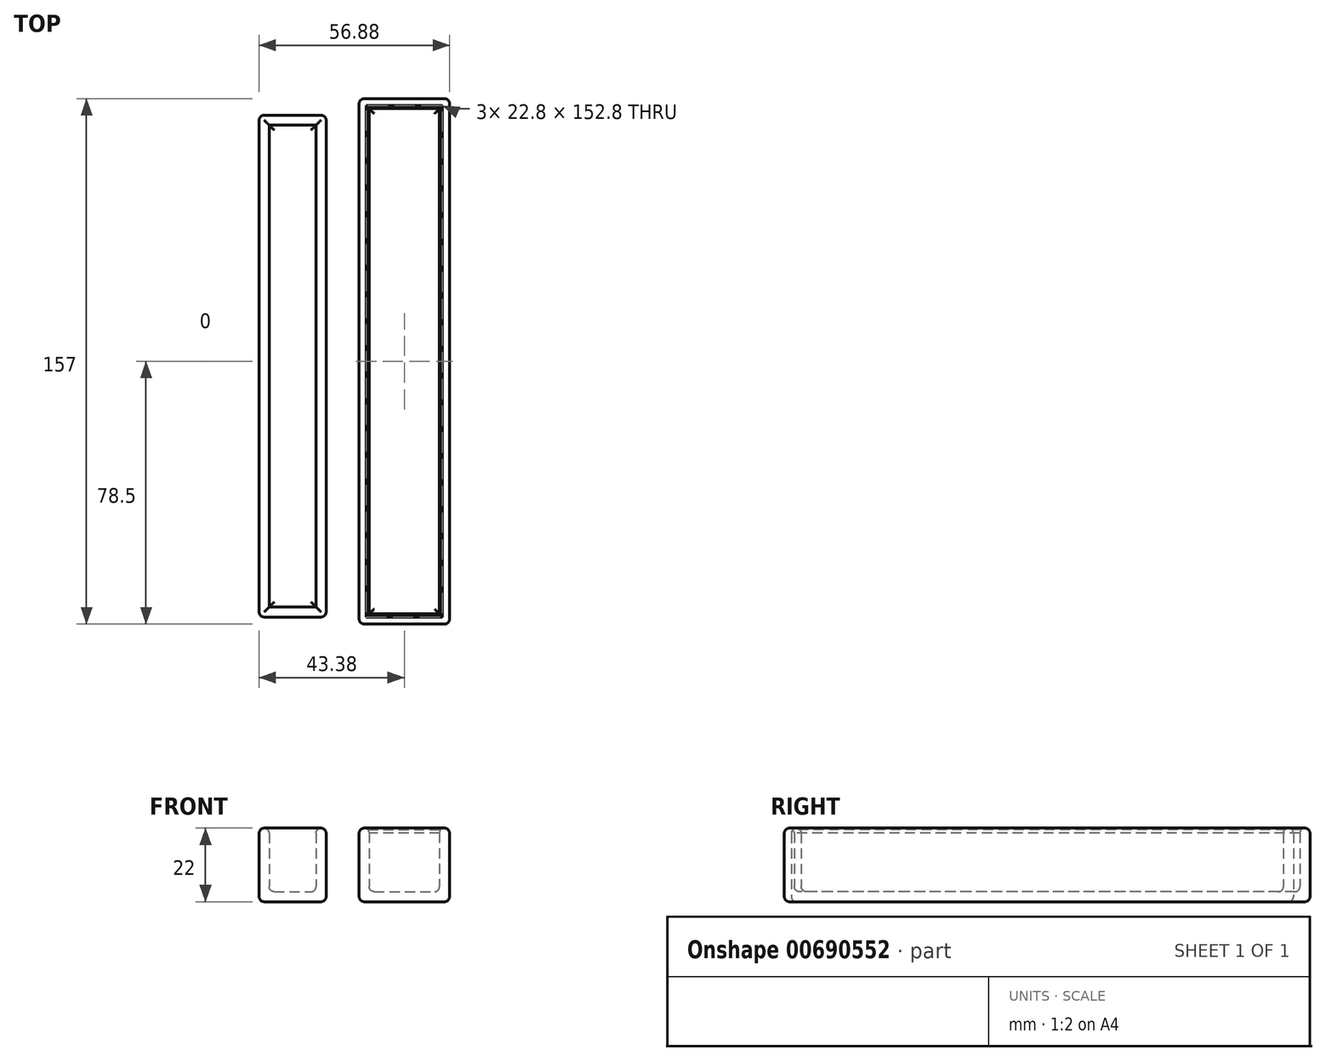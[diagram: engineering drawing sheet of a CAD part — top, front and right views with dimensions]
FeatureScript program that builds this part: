
annotation { "Feature Type Name" : "Feature", "Feature Type Description" : "" }
export const myFeature = defineFeature(function(context is Context, id is Id, definition is map)
    precondition{}
    {
        {
            var Q0;
            Q0=qCreatedBy(makeId("Top.planeOp"),FACE);
            var sketch = newSketch(context, id + "F0", { "sketchPlane" : qUnion([Q0])});
            skLineSegment(sketch, "E0.bottom", {"start": v(-39.88, 77.07) * mm, "end": v(-19.88, 77.07) * mm});
            skLineSegment(sketch, "E0.top", {"start": v(-39.88, -72.93) * mm, "end": v(-19.88, -72.93) * mm});
            skLineSegment(sketch, "E0.left", {"start": v(-39.88, 77.07) * mm, "end": v(-39.88, -72.93) * mm});
            skLineSegment(sketch, "E0.right", {"start": v(-19.88, 77.07) * mm, "end": v(-19.88, -72.93) * mm});
            skSolve(sketch);
        }
        {
            var Q0;
            Q0 = qSketchRegion(id + "F0", true);
            extrude(context, id + "F1", {"entities" : qUnion([Q0]), "depth" : 22 * mm, "offsetDistance" : 25 * mm});
        }
        {
            var Q0;
            Q0=makeQuery(id+"F1.opExtrude","CAP_FACE",FACE,{"disambiguationData":[OSD([sQuery(id+"F0.wireOp",EDGE,"E0.bottom"),sQuery(id+"F0.wireOp",EDGE,"E0.top"),sQuery(id+"F0.wireOp",EDGE,"E0.left"),sQuery(id+"F0.wireOp",EDGE,"E0.right")])],"isStart":false});
            shell(context, id + "F2", {"entities" : qUnion([Q0]), "thickness" : 3 * mm});
        }
        {
            var Q0;
            Q0=qCreatedBy(makeId("Top.planeOp"),FACE);
            var sketch = newSketch(context, id + "F3", { "sketchPlane" : qUnion([Q0])});
            skLineSegment(sketch, "E1.bottom", {"start": v(-10, 82) * mm, "end": v(17, 82) * mm});
            skLineSegment(sketch, "E1.top", {"start": v(-10, -75) * mm, "end": v(17, -75) * mm});
            skLineSegment(sketch, "E1.left", {"start": v(-10, 82) * mm, "end": v(-10, -75) * mm});
            skLineSegment(sketch, "E1.right", {"start": v(17, 82) * mm, "end": v(17, -75) * mm});
            skSolve(sketch);
        }
        {
            var Q0;
            Q0=makeQuery(id+"F3.imprint","IMPRINT",FACE,{"disambiguationData":[TD([[makeQuery(id+"F3.imprint","IMPRINT",EDGE,{"derivedFrom":sQuery(id+"F3.wireOp",EDGE,"E1.bottom")}),-1.0]])]});
            extrude(context, id + "F4", {"entities" : qUnion([Q0]), "depth" : 22 * mm, "offsetDistance" : 25 * mm});
        }
        {
            var Q0;
            Q0=makeQuery(id+"F4.opExtrude","CAP_FACE",FACE,{"disambiguationData":[OSD([sQuery(id+"F3.wireOp",EDGE,"E1.bottom"),sQuery(id+"F3.wireOp",EDGE,"E1.top"),sQuery(id+"F3.wireOp",EDGE,"E1.left"),sQuery(id+"F3.wireOp",EDGE,"E1.right")])],"isStart":false});
            shell(context, id + "F5", {"entities" : qUnion([Q0]), "thickness" : 3 * mm});
        }
        {
            var Q0;
            Q0=makeQuery(id+"F1.opExtrude","CAP_EDGE",EDGE,{"disambiguationData":[OSD([sQuery(id+"F0.wireOp",EDGE,"E0.right")])],"isStart":false});
            var Q1;
            {var subQ0=sQuery(id+"F0.wireOp",EDGE,"E0.right");Q1=makeQuery(id+"F2.opShell","OFFSET_EDGE",EDGE,{"disambiguationData":[OSD([subQ0]),TDD([makeQuery(id+"F1.opExtrude","CAP_EDGE",EDGE,{"disambiguationData":[OSD([subQ0])],"isStart":false})])]});}
            var Q2;
            Q2=makeQuery(id+"F1.opExtrude","CAP_EDGE",EDGE,{"disambiguationData":[OSD([sQuery(id+"F0.wireOp",EDGE,"E0.bottom")])],"isStart":false});
            var Q3;
            {var subQ0=sQuery(id+"F0.wireOp",EDGE,"E0.bottom");Q3=makeQuery(id+"F2.opShell","OFFSET_EDGE",EDGE,{"disambiguationData":[OSD([subQ0]),TDD([makeQuery(id+"F1.opExtrude","CAP_EDGE",EDGE,{"disambiguationData":[OSD([subQ0])],"isStart":false})])]});}
            var Q4;
            Q4=makeQuery(id+"F1.opExtrude","CAP_EDGE",EDGE,{"disambiguationData":[OSD([sQuery(id+"F0.wireOp",EDGE,"E0.left")])],"isStart":false});
            var Q5;
            {var subQ0=sQuery(id+"F0.wireOp",EDGE,"E0.left");Q5=makeQuery(id+"F2.opShell","OFFSET_EDGE",EDGE,{"disambiguationData":[OSD([subQ0]),TDD([makeQuery(id+"F1.opExtrude","CAP_EDGE",EDGE,{"disambiguationData":[OSD([subQ0])],"isStart":false})])]});}
            var Q6;
            {var subQ0=sQuery(id+"F0.wireOp",EDGE,"E0.top");Q6=makeQuery(id+"F2.opShell","OFFSET_EDGE",EDGE,{"disambiguationData":[OSD([subQ0]),TDD([makeQuery(id+"F1.opExtrude","CAP_EDGE",EDGE,{"disambiguationData":[OSD([subQ0])],"isStart":false})])]});}
            var Q7;
            Q7=makeQuery(id+"F1.opExtrude","CAP_EDGE",EDGE,{"disambiguationData":[OSD([sQuery(id+"F0.wireOp",EDGE,"E0.top")])],"isStart":false});
            var Q8;
            Q8=makeQuery(id+"F1.opExtrude","CAP_EDGE",EDGE,{"disambiguationData":[OSD([sQuery(id+"F0.wireOp",EDGE,"E0.left")])],"isStart":true});
            var Q9;
            Q9=makeQuery(id+"F1.opExtrude","SWEPT_EDGE",EDGE,{"disambiguationData":[OSD([sQuery(id+"F0.wireOp",EDGE,"E0.top"),sQuery(id+"F0.wireOp",EDGE,"E0.left")])]});
            var Q10;
            Q10=makeQuery(id+"F1.opExtrude","CAP_EDGE",EDGE,{"disambiguationData":[OSD([sQuery(id+"F0.wireOp",EDGE,"E0.top")])],"isStart":true});
            var Q11;
            Q11=makeQuery(id+"F1.opExtrude","SWEPT_EDGE",EDGE,{"disambiguationData":[OSD([sQuery(id+"F0.wireOp",EDGE,"E0.top"),sQuery(id+"F0.wireOp",EDGE,"E0.right")])]});
            var Q12;
            Q12=makeQuery(id+"F1.opExtrude","SWEPT_EDGE",EDGE,{"disambiguationData":[OSD([sQuery(id+"F0.wireOp",EDGE,"E0.bottom"),sQuery(id+"F0.wireOp",EDGE,"E0.right")])]});
            var Q13;
            Q13=makeQuery(id+"F1.opExtrude","SWEPT_EDGE",EDGE,{"disambiguationData":[OSD([sQuery(id+"F0.wireOp",EDGE,"E0.bottom"),sQuery(id+"F0.wireOp",EDGE,"E0.left")])]});
            var Q14;
            Q14=makeQuery(id+"F1.opExtrude","CAP_EDGE",EDGE,{"disambiguationData":[OSD([sQuery(id+"F0.wireOp",EDGE,"E0.bottom")])],"isStart":true});
            var Q15;
            Q15=makeQuery(id+"F1.opExtrude","CAP_EDGE",EDGE,{"disambiguationData":[OSD([sQuery(id+"F0.wireOp",EDGE,"E0.right")])],"isStart":true});
            var Q16;
            Q16=makeQuery(id+"F4.opExtrude","CAP_EDGE",EDGE,{"disambiguationData":[OSD([sQuery(id+"F3.wireOp",EDGE,"E1.bottom")])],"isStart":false});
            var Q17;
            Q17=makeQuery(id+"F4.opExtrude","CAP_EDGE",EDGE,{"disambiguationData":[OSD([sQuery(id+"F3.wireOp",EDGE,"E1.left")])],"isStart":false});
            var Q18;
            Q18=makeQuery(id+"F4.opExtrude","CAP_EDGE",EDGE,{"disambiguationData":[OSD([sQuery(id+"F3.wireOp",EDGE,"E1.right")])],"isStart":false});
            var Q19;
            Q19=makeQuery(id+"F4.opExtrude","CAP_EDGE",EDGE,{"disambiguationData":[OSD([sQuery(id+"F3.wireOp",EDGE,"E1.top")])],"isStart":false});
            var Q20;
            Q20=makeQuery(id+"F4.opExtrude","CAP_EDGE",EDGE,{"disambiguationData":[OSD([sQuery(id+"F3.wireOp",EDGE,"E1.top")])],"isStart":true});
            var Q21;
            Q21=makeQuery(id+"F4.opExtrude","SWEPT_EDGE",EDGE,{"disambiguationData":[OSD([sQuery(id+"F3.wireOp",EDGE,"E1.top"),sQuery(id+"F3.wireOp",EDGE,"E1.right")])]});
            var Q22;
            Q22=makeQuery(id+"F4.opExtrude","CAP_EDGE",EDGE,{"disambiguationData":[OSD([sQuery(id+"F3.wireOp",EDGE,"E1.right")])],"isStart":true});
            var Q23;
            Q23=makeQuery(id+"F4.opExtrude","CAP_EDGE",EDGE,{"disambiguationData":[OSD([sQuery(id+"F3.wireOp",EDGE,"E1.left")])],"isStart":true});
            var Q24;
            Q24=makeQuery(id+"F4.opExtrude","SWEPT_EDGE",EDGE,{"disambiguationData":[OSD([sQuery(id+"F3.wireOp",EDGE,"E1.top"),sQuery(id+"F3.wireOp",EDGE,"E1.left")])]});
            var Q25;
            Q25=makeQuery(id+"F4.opExtrude","SWEPT_EDGE",EDGE,{"disambiguationData":[OSD([sQuery(id+"F3.wireOp",EDGE,"E1.bottom"),sQuery(id+"F3.wireOp",EDGE,"E1.left")])]});
            var Q26;
            Q26=makeQuery(id+"F4.opExtrude","SWEPT_EDGE",EDGE,{"disambiguationData":[OSD([sQuery(id+"F3.wireOp",EDGE,"E1.bottom"),sQuery(id+"F3.wireOp",EDGE,"E1.right")])]});
            var Q27;
            Q27=makeQuery(id+"F4.opExtrude","CAP_EDGE",EDGE,{"disambiguationData":[OSD([sQuery(id+"F3.wireOp",EDGE,"E1.bottom")])],"isStart":true});
            var Q28;
            {var subQ0=sQuery(id+"F0.wireOp",EDGE,"E0.left");Q28=makeQuery(id+"F2.opShell","OFFSET_EDGE",EDGE,{"disambiguationData":[OSD([subQ0]),TDD([makeQuery(id+"F1.opExtrude","CAP_EDGE",EDGE,{"disambiguationData":[OSD([subQ0])],"isStart":true})])]});}
            var Q29;
            {var subQ0=sQuery(id+"F0.wireOp",EDGE,"E0.top");Q29=makeQuery(id+"F2.opShell","OFFSET_EDGE",EDGE,{"disambiguationData":[OSD([subQ0]),TDD([makeQuery(id+"F1.opExtrude","CAP_EDGE",EDGE,{"disambiguationData":[OSD([subQ0])],"isStart":true})])]});}
            var Q30;
            {var subQ0=sQuery(id+"F0.wireOp",EDGE,"E0.bottom");Q30=makeQuery(id+"F2.opShell","OFFSET_EDGE",EDGE,{"disambiguationData":[OSD([subQ0]),TDD([makeQuery(id+"F1.opExtrude","CAP_EDGE",EDGE,{"disambiguationData":[OSD([subQ0])],"isStart":true})])]});}
            var Q31;
            {var subQ0=sQuery(id+"F0.wireOp",EDGE,"E0.right");Q31=makeQuery(id+"F2.opShell","OFFSET_EDGE",EDGE,{"disambiguationData":[OSD([subQ0]),TDD([makeQuery(id+"F1.opExtrude","CAP_EDGE",EDGE,{"disambiguationData":[OSD([subQ0])],"isStart":true})])]});}
            var Q32;
            {var subQ0=sQuery(id+"F3.wireOp",EDGE,"E1.bottom");Q32=makeQuery(id+"F5.opShell","OFFSET_EDGE",EDGE,{"disambiguationData":[OSD([subQ0]),TDD([makeQuery(id+"F4.opExtrude","CAP_EDGE",EDGE,{"disambiguationData":[OSD([subQ0])],"isStart":true})])]});}
            var Q33;
            {var subQ0=sQuery(id+"F3.wireOp",EDGE,"E1.right");Q33=makeQuery(id+"F5.opShell","OFFSET_EDGE",EDGE,{"disambiguationData":[OSD([subQ0]),TDD([makeQuery(id+"F4.opExtrude","CAP_EDGE",EDGE,{"disambiguationData":[OSD([subQ0])],"isStart":true})])]});}
            var Q34;
            {var subQ0=sQuery(id+"F3.wireOp",EDGE,"E1.left");Q34=makeQuery(id+"F5.opShell","OFFSET_EDGE",EDGE,{"disambiguationData":[OSD([subQ0]),TDD([makeQuery(id+"F4.opExtrude","CAP_EDGE",EDGE,{"disambiguationData":[OSD([subQ0])],"isStart":true})])]});}
            var Q35;
            {var subQ0=sQuery(id+"F3.wireOp",EDGE,"E1.top");Q35=makeQuery(id+"F5.opShell","OFFSET_EDGE",EDGE,{"disambiguationData":[OSD([subQ0]),TDD([makeQuery(id+"F4.opExtrude","CAP_EDGE",EDGE,{"disambiguationData":[OSD([subQ0])],"isStart":true})])]});}
            fillet(context, id + "F6", {"entities" : qUnion([Q0, Q1, Q2, Q3, Q4, Q5, Q6, Q7, Q8, Q9, Q10, Q11, Q12, Q13, Q14, Q15, Q16, Q17, Q18, Q19, Q20, Q21, Q22, Q23, Q24, Q25, Q26, Q27, Q28, Q29, Q30, Q31, Q32, Q33, Q34, Q35]), "radius" : 1.5 * mm, "tangentPropagation" : true, "allowEdgeOverflow" : false});
        }
        {
            var Q0;
            {var subQ0=sQuery(id+"F3.wireOp",EDGE,"E1.bottom");Q0=makeQuery(id+"F5.opShell","OFFSET_EDGE",EDGE,{"disambiguationData":[OSD([subQ0]),TDD([makeQuery(id+"F4.opExtrude","CAP_EDGE",EDGE,{"disambiguationData":[OSD([subQ0])],"isStart":false})])]});}
            var Q1;
            {var subQ0=sQuery(id+"F3.wireOp",EDGE,"E1.left");Q1=makeQuery(id+"F5.opShell","OFFSET_EDGE",EDGE,{"disambiguationData":[OSD([subQ0]),TDD([makeQuery(id+"F4.opExtrude","CAP_EDGE",EDGE,{"disambiguationData":[OSD([subQ0])],"isStart":false})])]});}
            var Q2;
            {var subQ0=sQuery(id+"F3.wireOp",EDGE,"E1.right");Q2=makeQuery(id+"F5.opShell","OFFSET_EDGE",EDGE,{"disambiguationData":[OSD([subQ0]),TDD([makeQuery(id+"F4.opExtrude","CAP_EDGE",EDGE,{"disambiguationData":[OSD([subQ0])],"isStart":false})])]});}
            var Q3;
            {var subQ0=sQuery(id+"F3.wireOp",EDGE,"E1.top");Q3=makeQuery(id+"F5.opShell","OFFSET_EDGE",EDGE,{"disambiguationData":[OSD([subQ0]),TDD([makeQuery(id+"F4.opExtrude","CAP_EDGE",EDGE,{"disambiguationData":[OSD([subQ0])],"isStart":false})])]});}
            chamfer(context, id + "F7", {"entities" : qUnion([Q0, Q1, Q2, Q3]), "width" : .9 * mm, "tangentPropagation" : true});
        }
        {
            var Q0;
            {var subQ0=sQuery(id+"F3.wireOp",EDGE,"E1.bottom");Q0=makeQuery(id+"F7.opChamfer","BLEND_EDGE",EDGE,{"blendedFrom":[makeQuery(id+"F5.opShell","OFFSET_EDGE",EDGE,{"disambiguationData":[OSD([subQ0]),TDD([makeQuery(id+"F4.opExtrude","CAP_EDGE",EDGE,{"disambiguationData":[OSD([subQ0])],"isStart":false})])]}),makeQuery(id+"F5.opShell","OFFSET_FACE",FACE,{"disambiguationData":[OSD([subQ0])]})],"blendedInto":[makeQuery(id+"F5.opShell","OFFSET_FACE",FACE,{"disambiguationData":[OSD([subQ0])]})]});}
            var Q1;
            {var subQ0=sQuery(id+"F3.wireOp",EDGE,"E1.left");Q1=makeQuery(id+"F7.opChamfer","BLEND_EDGE",EDGE,{"blendedFrom":[makeQuery(id+"F5.opShell","OFFSET_EDGE",EDGE,{"disambiguationData":[OSD([subQ0]),TDD([makeQuery(id+"F4.opExtrude","CAP_EDGE",EDGE,{"disambiguationData":[OSD([subQ0])],"isStart":false})])]}),makeQuery(id+"F5.opShell","OFFSET_FACE",FACE,{"disambiguationData":[OSD([subQ0])]})],"blendedInto":[makeQuery(id+"F5.opShell","OFFSET_FACE",FACE,{"disambiguationData":[OSD([subQ0])]})]});}
            var Q2;
            {var subQ0=sQuery(id+"F3.wireOp",EDGE,"E1.right");Q2=makeQuery(id+"F7.opChamfer","BLEND_EDGE",EDGE,{"blendedFrom":[makeQuery(id+"F5.opShell","OFFSET_EDGE",EDGE,{"disambiguationData":[OSD([subQ0]),TDD([makeQuery(id+"F4.opExtrude","CAP_EDGE",EDGE,{"disambiguationData":[OSD([subQ0])],"isStart":false})])]}),makeQuery(id+"F5.opShell","OFFSET_FACE",FACE,{"disambiguationData":[OSD([subQ0])]})],"blendedInto":[makeQuery(id+"F5.opShell","OFFSET_FACE",FACE,{"disambiguationData":[OSD([subQ0])]})]});}
            var Q3;
            {var subQ0=sQuery(id+"F3.wireOp",EDGE,"E1.top");Q3=makeQuery(id+"F7.opChamfer","BLEND_EDGE",EDGE,{"blendedFrom":[makeQuery(id+"F5.opShell","OFFSET_EDGE",EDGE,{"disambiguationData":[OSD([subQ0]),TDD([makeQuery(id+"F4.opExtrude","CAP_EDGE",EDGE,{"disambiguationData":[OSD([subQ0])],"isStart":false})])]}),makeQuery(id+"F5.opShell","OFFSET_FACE",FACE,{"disambiguationData":[OSD([subQ0])]})],"blendedInto":[makeQuery(id+"F5.opShell","OFFSET_FACE",FACE,{"disambiguationData":[OSD([subQ0])]})]});}
            chamfer(context, id + "F8", {"entities" : qUnion([Q0, Q1, Q2, Q3]), "width" : 1.3 * mm, "tangentPropagation" : true});
        }
    });
